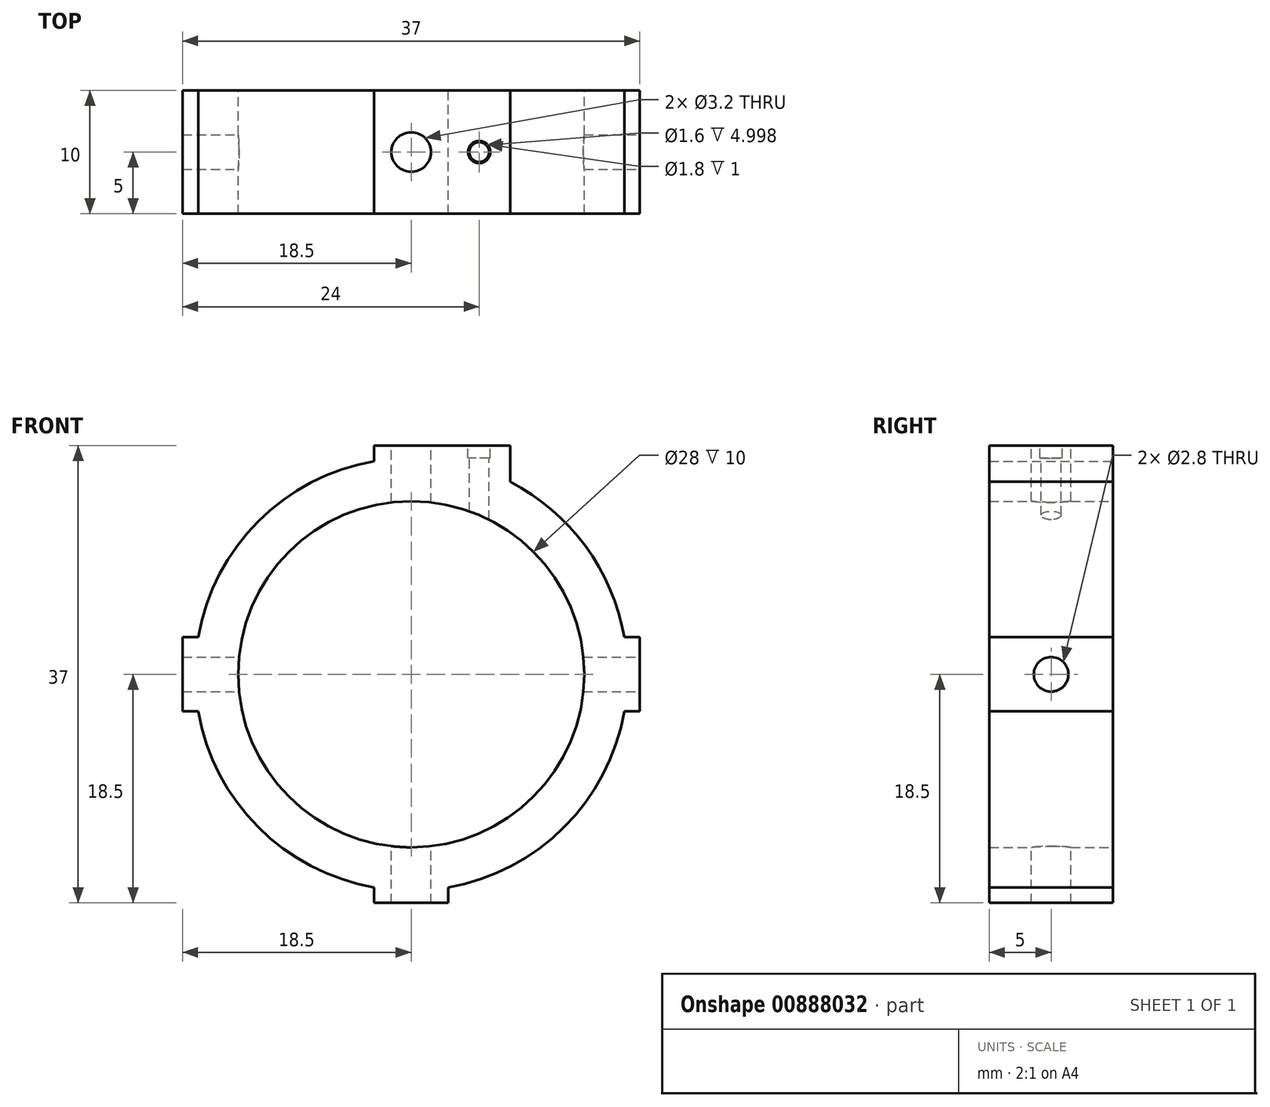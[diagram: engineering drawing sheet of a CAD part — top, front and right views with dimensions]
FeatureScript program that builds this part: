
annotation { "Feature Type Name" : "Feature", "Feature Type Description" : "" }
export const myFeature = defineFeature(function(context is Context, id is Id, definition is map)
    precondition{}
    {
        {
            var Q0;
            Q0=qCreatedBy(makeId("Front.planeOp"),FACE);
            var sketch = newSketch(context, id + "F0", { "sketchPlane" : qUnion([Q0])});
            skCircle(sketch, "E0", {"center": v(0, 0) * mm, "radius": 14 * mm});
            skCircle(sketch, "E1", {"center": v(0, 0) * mm, "radius": 17.5 * mm});
            skLineSegment(sketch, "E2.bottom", {"start": v(-3, 18.5) * mm, "end": v(3, 18.5) * mm});
            skLineSegment(sketch, "E2.top", {"start": v(-3, -18.5) * mm, "end": v(3, -18.5) * mm});
            skLineSegment(sketch, "E2.left", {"start": v(-3, 18.5) * mm, "end": v(-3, -18.5) * mm});
            skLineSegment(sketch, "E2.right", {"start": v(3, 18.5) * mm, "end": v(3, -18.5) * mm});
            skLineSegment(sketch, "E3.bottom", {"start": v(18.5, -3) * mm, "end": v(-18.5, -3) * mm});
            skLineSegment(sketch, "E3.top", {"start": v(18.5, 3) * mm, "end": v(-18.5, 3) * mm});
            skLineSegment(sketch, "E3.left", {"start": v(18.5, -3) * mm, "end": v(18.5, 3) * mm});
            skLineSegment(sketch, "E3.right", {"start": v(-18.5, -3) * mm, "end": v(-18.5, 3) * mm});
            skSolve(sketch);
        }
        {
            var Q0;
            Q0=qSketchRegion(id+"F0",true);
            extrude(context, id + "F1", {"entities" : qUnion([Q0]), "depth" : 10 * mm, "offsetDistance" : 25 * mm});
        }
        {
            var Q0;
            Q0=makeQuery(id+"F1.opExtrude","SWEPT_FACE",FACE,{"disambiguationData":[OSD([sQuery(id+"F0.wireOp",EDGE,"E2.bottom")])]});
            var sketch = newSketch(context, id + "F2", { "sketchPlane" : qUnion([Q0])});
            skCircle(sketch, "E4", {"center": v(0, -5) * mm, "radius": 1.6 * mm});
            skSolve(sketch);
        }
        {
            var Q0;
            Q0=qSketchRegion(id+"F2",true);
            extrude(context, id + "F3", {"entities" : qUnion([Q0]), "operationType" : NewBodyOperationType.REMOVE, "oppositeDirection" : true, "depth" : 40 * mm, "offsetDistance" : 25 * mm});
        }
        {
            var Q0;
            Q0=makeQuery(id+"F1.opExtrude","SWEPT_FACE",FACE,{"disambiguationData":[OSD([sQuery(id+"F0.wireOp",EDGE,"E3.left")])]});
            var sketch = newSketch(context, id + "F4", { "sketchPlane" : qUnion([Q0])});
            skCircle(sketch, "E5", {"center": v(-5, 0) * mm, "radius": 1.4 * mm});
            skSolve(sketch);
        }
        {
            var Q0;
            Q0=qSketchRegion(id+"F4",true);
            extrude(context, id + "F5", {"entities" : qUnion([Q0]), "operationType" : NewBodyOperationType.REMOVE, "oppositeDirection" : true, "depth" : 40 * mm, "offsetDistance" : 25 * mm});
        }
        {
            var Q0;
            Q0=makeQuery(id+"F1.opExtrude","SWEPT_FACE",FACE,{"disambiguationData":[OSD([sQuery(id+"F0.wireOp",EDGE,"E2.bottom")])]});
            var sketch = newSketch(context, id + "F6", { "sketchPlane" : qUnion([Q0])});
            skLineSegment(sketch, "E6.bottom", {"start": v(3, 0) * mm, "end": v(8, 0) * mm});
            skLineSegment(sketch, "E6.top", {"start": v(3, -10) * mm, "end": v(8, -10) * mm});
            skLineSegment(sketch, "E6.left", {"start": v(3, 0) * mm, "end": v(3, -10) * mm});
            skLineSegment(sketch, "E6.right", {"start": v(8, 0) * mm, "end": v(8, -10) * mm});
            skSolve(sketch);
        }
        {
            var Q0;
            Q0=qSketchRegion(id+"F6",true);
            extrude(context, id + "F7", {"entities" : qUnion([Q0]), "operationType" : NewBodyOperationType.ADD, "depth" : -4 * mm, "offsetDistance" : 25 * mm});
        }
        {
            var Q0;
            Q0=makeQuery(id+"F7.boolean.opBoolean","MERGE",FACE,{"derivedFrom":[makeQuery(id+"F1.opExtrude","SWEPT_FACE",FACE,{"disambiguationData":[OSD([sQuery(id+"F0.wireOp",EDGE,"E2.bottom")])]}),makeQuery(id+"F7.opExtrude","CAP_FACE",FACE,{"disambiguationData":[OSD([sQuery(id+"F6.wireOp",EDGE,"E6.bottom"),sQuery(id+"F6.wireOp",EDGE,"E6.top"),sQuery(id+"F6.wireOp",EDGE,"E6.left"),sQuery(id+"F6.wireOp",EDGE,"E6.right")])],"isStart":true})]});
            var sketch = newSketch(context, id + "F8", { "sketchPlane" : qUnion([Q0])});
            skCircle(sketch, "E7", {"center": v(5.5, -5) * mm, "radius": 0.8 * mm});
            skPoint(sketch, "E7.centerSnap0", {"position": v(-3, -5) * mm});
            skSolve(sketch);
        }
        {
            var Q0;
            Q0=qSketchRegion(id+"F8",true);
            extrude(context, id + "F9", {"entities" : qUnion([Q0]), "operationType" : NewBodyOperationType.REMOVE, "oppositeDirection" : true, "depth" : 7 * mm, "offsetDistance" : 25 * mm});
        }
        {
            var Q0;
            Q0=makeQuery(id+"F7.boolean.opBoolean","MERGE",FACE,{"derivedFrom":[makeQuery(id+"F1.opExtrude","SWEPT_FACE",FACE,{"disambiguationData":[OSD([sQuery(id+"F0.wireOp",EDGE,"E2.bottom")])]}),makeQuery(id+"F7.opExtrude","CAP_FACE",FACE,{"disambiguationData":[OSD([sQuery(id+"F6.wireOp",EDGE,"E6.bottom"),sQuery(id+"F6.wireOp",EDGE,"E6.top"),sQuery(id+"F6.wireOp",EDGE,"E6.left"),sQuery(id+"F6.wireOp",EDGE,"E6.right")])],"isStart":true})]});
            var sketch = newSketch(context, id + "F10", { "sketchPlane" : qUnion([Q0])});
            skCircle(sketch, "E8", {"center": v(5.5, -5) * mm, "radius": 0.9 * mm});
            skSolve(sketch);
        }
        {
            var Q0;
            Q0=qSketchRegion(id+"F10",true);
            extrude(context, id + "F11", {"entities" : qUnion([Q0]), "operationType" : NewBodyOperationType.REMOVE, "oppositeDirection" : true, "depth" : 1 * mm, "offsetDistance" : 25 * mm});
        }
    });
